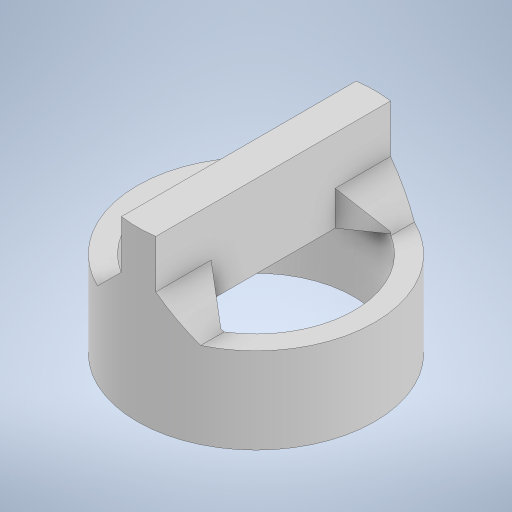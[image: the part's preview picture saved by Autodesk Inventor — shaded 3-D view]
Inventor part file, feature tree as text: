
AUTODESK INVENTOR PART (.ipt)
format: ipt  version: 2024 (Build 280153000, 153)  size: 248,320 bytes
history: native  units: mm
features: extrude x2, chamfer x2, other x1
ambient origin geometry x8: Origin, YZ Plane, XZ Plane, XY Plane, X Axis, Y Axis, Z Axis, Center Point
bodies: Body1 (feature_tree)
feature tree (5):
  other  "솔리드1"
  extrude  "돌출1"  Depth=5.7mm
  extrude  "돌출2"  Depth=6.9mm
  chamfer  "모따기1"  Distance=2.5mm
  chamfer  "모따기2"  Distance=1.0mm
